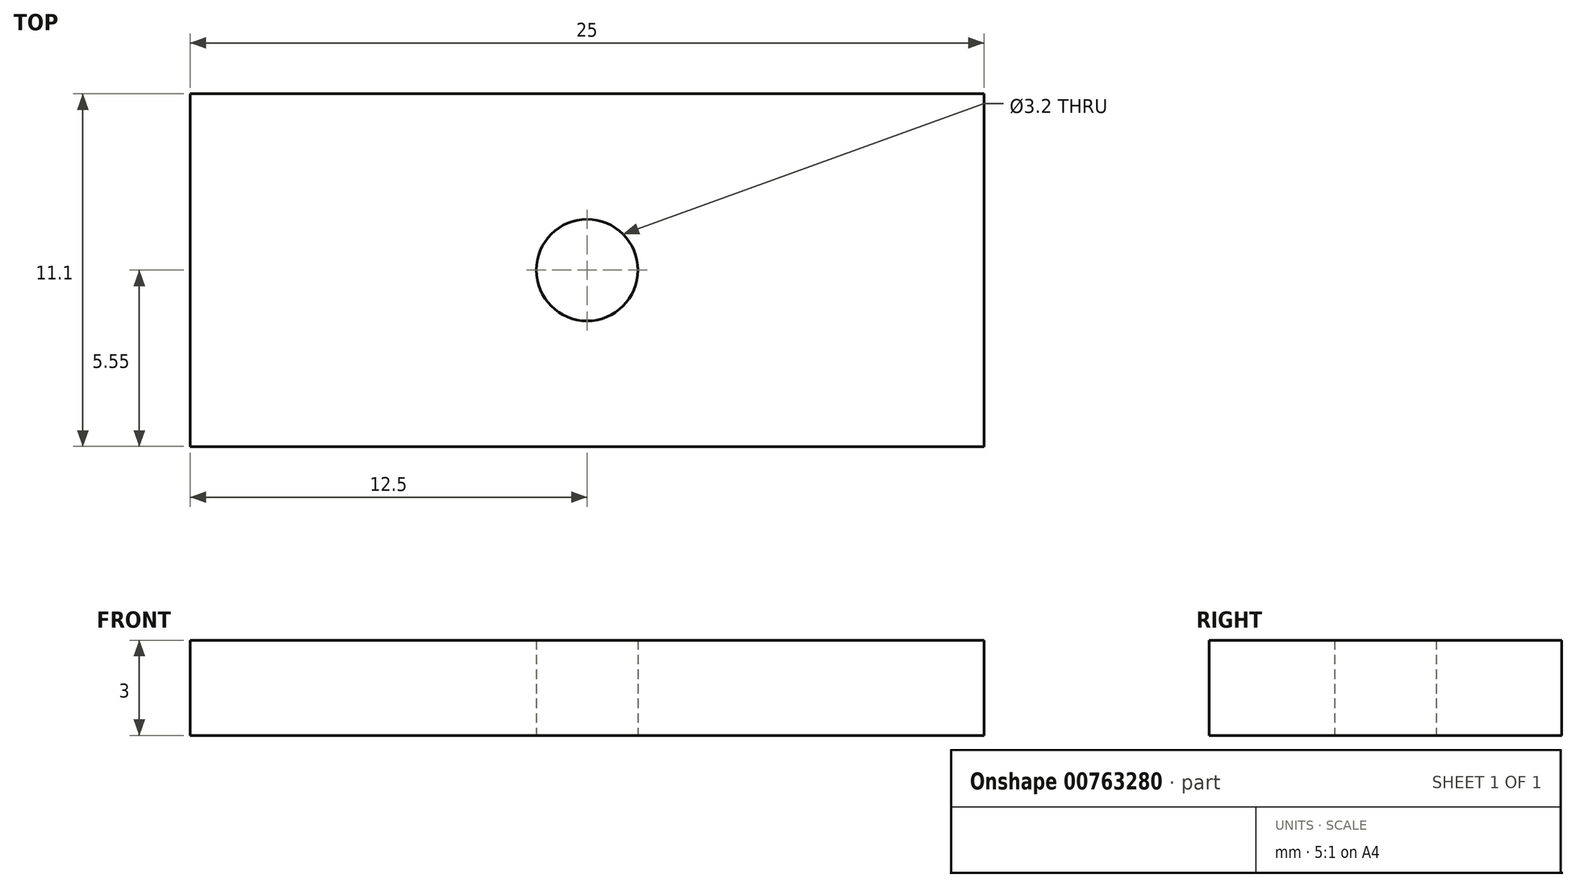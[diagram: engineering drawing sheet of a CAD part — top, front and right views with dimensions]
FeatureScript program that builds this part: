
annotation { "Feature Type Name" : "Feature", "Feature Type Description" : "" }
export const myFeature = defineFeature(function(context is Context, id is Id, definition is map)
    precondition{}
    {
        {
            var Q0;
            Q0=qCreatedBy(makeId("Top.planeOp"),FACE);
            var sketch = newSketch(context, id + "F0", { "sketchPlane" : qUnion([Q0])});
            skLineSegment(sketch, "E0.bottom", {"start": v(-12.5, 5.55) * mm, "end": v(12.5, 5.55) * mm});
            skLineSegment(sketch, "E0.top", {"start": v(-12.5, -5.55) * mm, "end": v(12.5, -5.55) * mm});
            skLineSegment(sketch, "E0.left", {"start": v(-12.5, 5.55) * mm, "end": v(-12.5, -5.55) * mm});
            skLineSegment(sketch, "E0.right", {"start": v(12.5, 5.55) * mm, "end": v(12.5, -5.55) * mm});
            skPoint(sketch, "E0.middle", {"position": v(0, 0) * mm});
            skCircle(sketch, "E1", {"center": v(0, 0) * mm, "radius": 1.6 * mm});
            skSolve(sketch);
        }
        {
            var Q0;
            Q0=makeQuery(id+"F0.imprint","IMPRINT",FACE,{"disambiguationData":[TD([[makeQuery(id+"F0.imprint","IMPRINT",EDGE,{"derivedFrom":sQuery(id+"F0.wireOp",EDGE,"E0.bottom")}),-1.0]])]});
            extrude(context, id + "F1", {"entities" : qUnion([Q0]), "depth" : 3 * mm, "offsetDistance" : 25 * mm});
        }
    });
